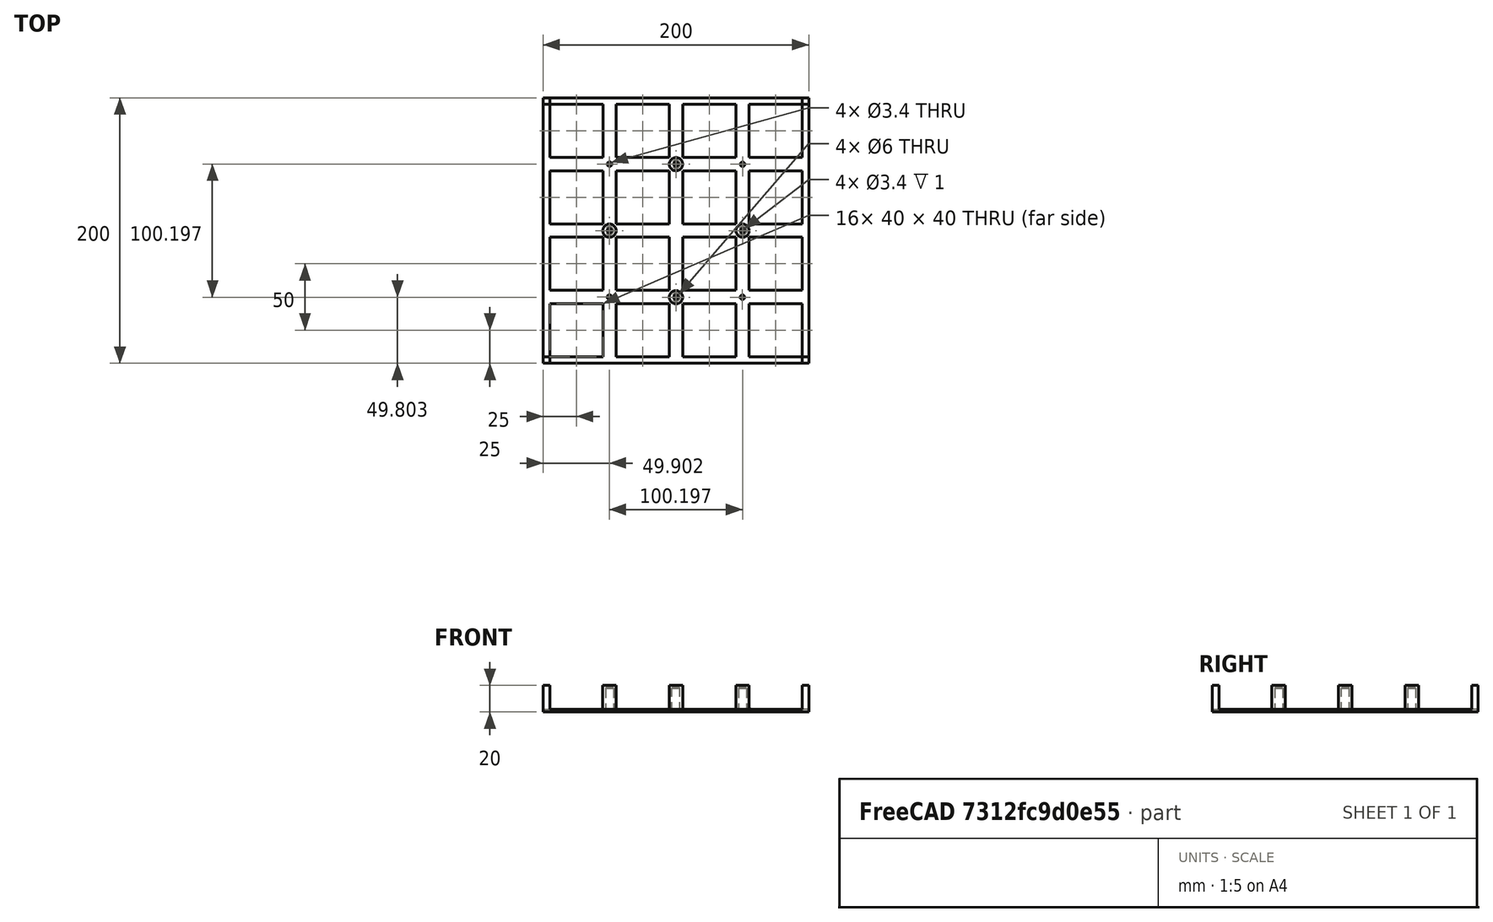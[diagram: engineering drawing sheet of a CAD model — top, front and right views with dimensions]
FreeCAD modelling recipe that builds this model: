
FCSTD DOCUMENT  (FreeCAD 0.19R23578 (Git))
Label: case
License: All rights reserved
LicenseURL: http://en.wikipedia.org/wiki/All_rights_reserved
objects: Sketcher::SketchObject×7, PartDesign::Pad×3, PartDesign::PolarPattern×3, PartDesign::Pocket×2, PartDesign::Hole×2, PartDesign::LinearPattern×2, Mesh::Feature×1, PartDesign::Body×1, PartDesign::Line×1, PartDesign::MultiTransform×1, PartDesign::Chamfer×1, PartDesign::Fillet×1
note: 33 computed .brp shape members not serialized (recipe doc carries the construction recipe); baked Part::Feature solids carry a one-line shape summary decoded from their .brp

FEATURE [Sketcher::SketchObject] Sketch
  MapMode = 5
  Support = -> [XY_Plane]
  sketch-geometry (4):
    g0: LineSegment StartX=0 StartY=0 StartZ=0 EndX=200 EndY=0 EndZ=0
    g1: LineSegment StartX=200 StartY=0 StartZ=0 EndX=200 EndY=-200 EndZ=0
    g2: LineSegment StartX=200 StartY=-200 StartZ=0 EndX=0 EndY=-200 EndZ=0
    g3: LineSegment StartX=0 StartY=-200 StartZ=0 EndX=0 EndY=0 EndZ=0
  constraints (11):
    c: Coincident(g0,g1)
    c: Coincident(g1,g2)
    c: Coincident(g2,g3)
    c: Coincident(g3,g0)
    c: Horizontal(g0)
    c: Horizontal(g2)
    c: Vertical(g1)
    c: Vertical(g3)
    c: Coincident(g0,g-1)
    c: DistanceX(g0,g0) = 200
    c: DistanceY(g3,g3) = 200
FEATURE [PartDesign::Pad] Pad
  Direction = (1,1,1)
  Length = 2
  Length2 = 100
  Profile = -> Sketch
  Type = 0
FEATURE [Sketcher::SketchObject] Sketch001
  MapMode = 5
  Placement = pos=(0,0,2) rot=(0,0,1;0rad)
  Support = -> [Pad]
  sketch-geometry (1):
    g0: Circle CenterX=100 CenterY=-50 CenterZ=0 NormalX=0 NormalY=0 NormalZ=1 AngleXU=0 Radius=5
  constraints (3):
    c: DistanceY(g-1,g0) = -50
    c: DistanceX(g-2,g0) = 100
    c: Diameter(g0) = 10
FEATURE [PartDesign::Pad] Pad001
  BaseFeature = -> Pad
  Direction = (1,1,1)
  Length = 18
  Length2 = 100
  Profile = -> Sketch001
  Type = 0
FEATURE [Sketcher::SketchObject] Sketch002
  MapMode = 5
  Placement = pos=(0,0,0) rot=(1,0,0;3.14159rad)
  Support = -> [Pad001]
  sketch-geometry (1):
    g0: Circle CenterX=100 CenterY=50 CenterZ=0 NormalX=0 NormalY=0 NormalZ=1 AngleXU=0 Radius=3
  constraints (3):
    c: DistanceX(g-2,g0) = 100
    c: DistanceY(g-1,g0) = 50
    c: Diameter(g0) = 6
FEATURE [PartDesign::Pocket] Pocket
  BaseFeature = -> Pad001
  Length = 19
  Length2 = 100
  Profile = -> Sketch002
  Type = 0
FEATURE [Sketcher::SketchObject] Sketch003
  MapMode = 5
  Placement = pos=(0,0,20) rot=(0,0,1;0rad)
  Support = -> [Pocket]
  sketch-geometry (1):
    g0: Circle CenterX=100 CenterY=-50 CenterZ=0 NormalX=0 NormalY=0 NormalZ=1 AngleXU=0 Radius=1.7
  constraints (3):
    c: DistanceY(g-1,g0) = -50
    c: DistanceX(g-2,g0) = 100
    c: Diameter(g0) = 3.4
FEATURE [PartDesign::Hole] Hole
  BaseFeature = -> Pocket
  Depth = 25
  DepthType = 1
  Diameter = 3.4
  DrillPoint = 1
  DrillPointAngle = 118
  HoleCutCountersinkAngle = 90
  HoleCutDepth = 0
  HoleCutDiameter = 0
  HoleCutType = 0
  ModelActualThread = false
  Profile = -> Sketch003
  Tapered = false
  TaperedAngle = 90
  ThreadAngle = 0
  ThreadClass = 0
  ThreadCutOffInner = 0
  ThreadCutOffOuter = 0
  ThreadDirection = 0
  ThreadFit = 0
  ThreadPitch = 0
  ThreadSize = 9
  ThreadType = 1
  Threaded = false
FEATURE [Sketcher::SketchObject] Sketch005
  MapMode = 5
  Placement = pos=(0,0,-2) rot=(1,0,0;3.14159rad)
  sketch-geometry (1):
    g0: Circle CenterX=50 CenterY=50 CenterZ=0 NormalX=0 NormalY=0 NormalZ=1 AngleXU=0 Radius=1.7
  constraints (3):
    c: DistanceX(g-2,g0) = 50
    c: DistanceY(g-1,g0) = 50
    c: Diameter(g0) = 3.4
FEATURE [PartDesign::LinearPattern] LinearPattern
  Direction = -> X_Axis
  Length = 150
  Occurrences = 4
FEATURE [PartDesign::LinearPattern] LinearPattern001
  Direction = -> Y_Axis
  Length = 150
  Occurrences = 4
  Reversed = true
FEATURE [Mesh::Feature] Mesh  label="Body (Meshed)"
FEATURE [PartDesign::Body] Body
  Group = -> [Sketch,Pad,Sketch001,Pad001,Sketch002,Pocket,Sketch003,Hole,DatumLine,PolarPattern,Sketch005,Hole001,PolarPattern001,Sketch006,Pocket001,MultiTransform,LinearPattern,LinearPattern001,Chamfer,Fillet,Sketch007,Pad002,PolarPattern002]
  Origin = -> Origin
  Tip = -> PolarPattern002
FEATURE [PartDesign::Line] DatumLine
  AttacherType = Attacher::AttachEngineLine
  AttachmentOffset = pos=(100,-100,0) rot=(0,0,1;0rad)
  Length = 20
  MapMode = 18
  Placement = pos=(100,-100,0) rot=(0,0,1;0rad)
  ResizeMode = 0
  Support = -> [Body]
FEATURE [PartDesign::PolarPattern] PolarPattern
  Angle = 360
  Axis = -> DatumLine
  BaseFeature = -> Hole
  Occurrences = 4
  Originals = -> [Pad001,Pocket,Hole]
FEATURE [PartDesign::Hole] Hole001
  BaseFeature = -> PolarPattern
  Depth = 25
  DepthType = 1
  Diameter = 3.4
  DrillPoint = 1
  DrillPointAngle = 118
  HoleCutCountersinkAngle = 90
  HoleCutDepth = 0
  HoleCutDiameter = 0
  HoleCutType = 0
  ModelActualThread = false
  Profile = -> Sketch005
  Tapered = false
  TaperedAngle = 90
  ThreadAngle = 0
  ThreadClass = 0
  ThreadCutOffInner = 0
  ThreadCutOffOuter = 0
  ThreadDirection = 0
  ThreadFit = 0
  ThreadPitch = 0
  ThreadSize = 9
  ThreadType = 1
  Threaded = false
FEATURE [PartDesign::PolarPattern] PolarPattern001
  Angle = 360
  Axis = -> DatumLine
  BaseFeature = -> Hole001
  Occurrences = 4
  Originals = -> [Hole001]
FEATURE [Sketcher::SketchObject] Sketch006
  MapMode = 5
  Placement = pos=(0,0,2) rot=(0,0,1;0rad)
  Support = -> [PolarPattern001]
  sketch-geometry (4):
    g0: LineSegment StartX=5 StartY=-5 StartZ=0 EndX=45 EndY=-5 EndZ=0
    g1: LineSegment StartX=45 StartY=-5 StartZ=0 EndX=45 EndY=-45 EndZ=0
    g2: LineSegment StartX=45 StartY=-45 StartZ=0 EndX=5 EndY=-45 EndZ=0
    g3: LineSegment StartX=5 StartY=-45 StartZ=0 EndX=5 EndY=-5 EndZ=0
  constraints (12):
    c: Coincident(g0,g1)
    c: Coincident(g1,g2)
    c: Coincident(g2,g3)
    c: Coincident(g3,g0)
    c: Horizontal(g0)
    c: Horizontal(g2)
    c: Vertical(g1)
    c: Vertical(g3)
    c: DistanceX(g0,g0) = 40
    c: DistanceY(g3,g3) = 40
    c: DistanceX(g-2,g0) = 5
    c: DistanceY(g-1,g0) = -5
FEATURE [PartDesign::Pocket] Pocket001
  BaseFeature = -> PolarPattern001
  Length = 5
  Length2 = 100
  Profile = -> Sketch006
  Type = 1
FEATURE [PartDesign::MultiTransform] MultiTransform
  BaseFeature = -> Pocket001
  Originals = -> [Pocket001]
  Transformations = -> [LinearPattern,LinearPattern001]
FEATURE [PartDesign::Chamfer] Chamfer
  Angle = 52
  Base = -> MultiTransform [Edge223,Edge196,Edge181,Edge171]
  BaseFeature = -> MultiTransform
  ChamferType = 2
  FlipDirection = false
  Size = 1
  Size2 = 1
  SupportTransform = false
FEATURE [PartDesign::Fillet] Fillet
  Base = -> Chamfer [Edge236,Edge237,Edge235,Edge234]
  BaseFeature = -> Chamfer
  Radius = 1.5
  SupportTransform = false
FEATURE [Sketcher::SketchObject] Sketch007
  MapMode = 5
  Placement = pos=(0,0,2) rot=(0,0,1;0rad)
  Support = -> [Fillet]
  sketch-geometry (4):
    g0: LineSegment StartX=0 StartY=0 StartZ=0 EndX=5 EndY=0 EndZ=0
    g1: LineSegment StartX=5 StartY=0 StartZ=0 EndX=5 EndY=-5 EndZ=0
    g2: LineSegment StartX=5 StartY=-5 StartZ=0 EndX=0 EndY=-5 EndZ=0
    g3: LineSegment StartX=0 StartY=-5 StartZ=0 EndX=0 EndY=0 EndZ=0
  constraints (11):
    c: Coincident(g0,g1)
    c: Coincident(g1,g2)
    c: Coincident(g2,g3)
    c: Coincident(g3,g0)
    c: Horizontal(g0)
    c: Horizontal(g2)
    c: Vertical(g1)
    c: Vertical(g3)
    c: Coincident(g0,g-1)
    c: DistanceX(g0,g0) = 5
    c: DistanceY(g3,g3) = 5
FEATURE [PartDesign::Pad] Pad002
  BaseFeature = -> Fillet
  Direction = (1,1,1)
  Length = 18
  Length2 = 100
  Profile = -> Sketch007
  Type = 0
FEATURE [PartDesign::PolarPattern] PolarPattern002
  Angle = 360
  Axis = -> DatumLine
  BaseFeature = -> Pad002
  Occurrences = 4
  Originals = -> [Pad002]
